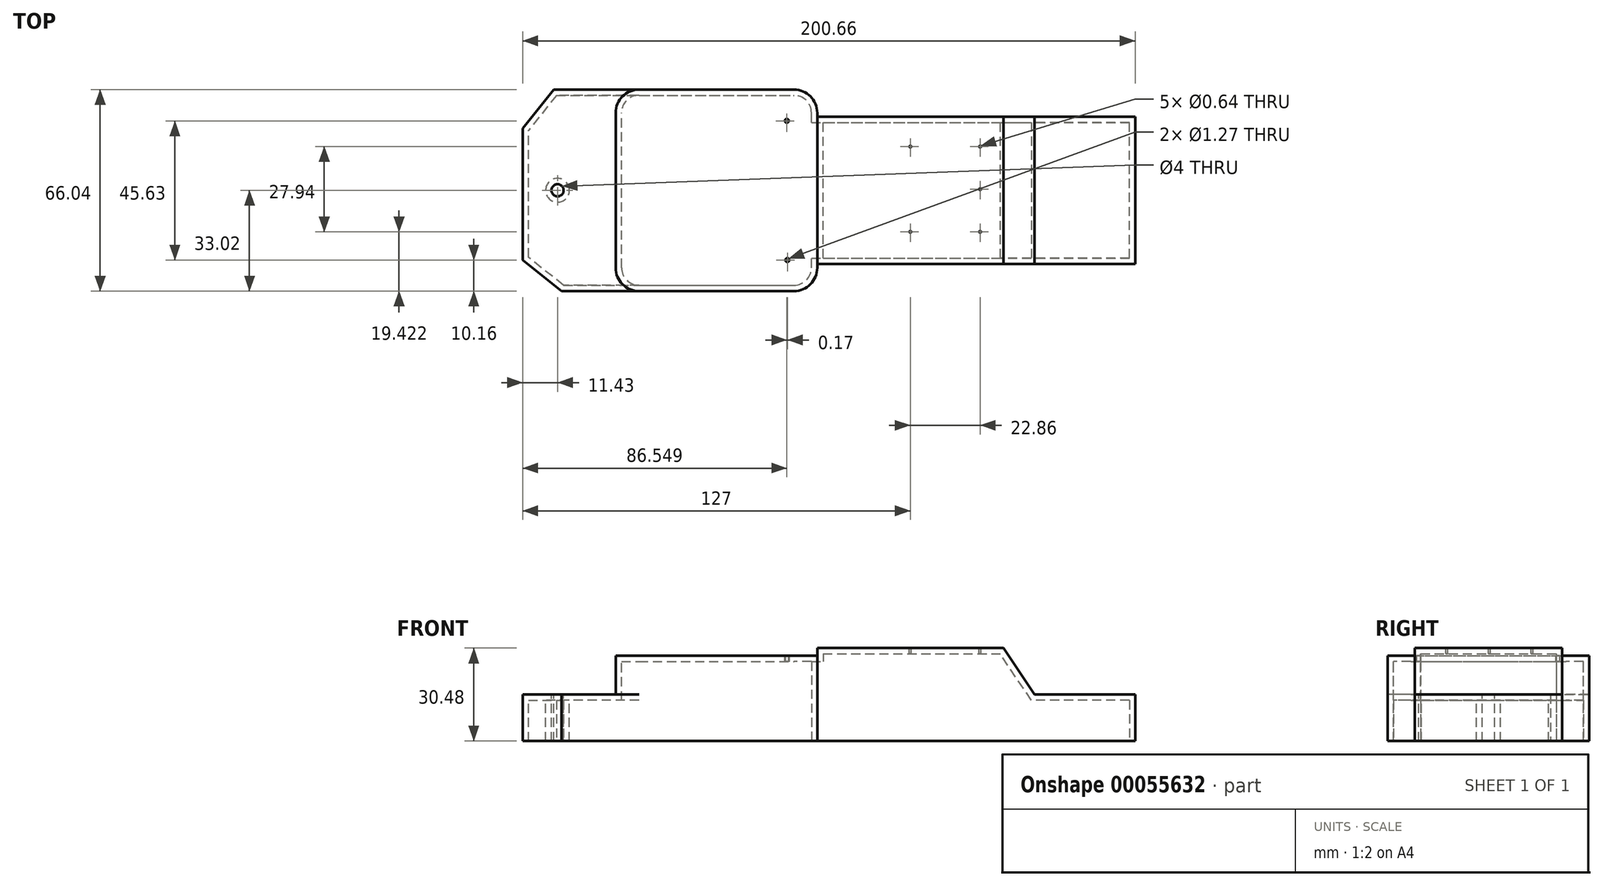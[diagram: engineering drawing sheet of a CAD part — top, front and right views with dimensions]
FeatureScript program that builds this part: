
annotation { "Feature Type Name" : "Feature", "Feature Type Description" : "" }
export const myFeature = defineFeature(function(context is Context, id is Id, definition is map)
    precondition{}
    {
        {
            var Q0;
            Q0=qCreatedBy(makeId("Top.planeOp"),FACE);
            var sketch = newSketch(context, id + "F0", { "sketchPlane" : qUnion([Q0])});
            skLineSegment(sketch, "E0.bottom", {"start": v(0, 0) * mm, "end": v(66.04, 0) * mm});
            skLineSegment(sketch, "E0.top", {"start": v(0, 66.04) * mm, "end": v(66.04, 66.04) * mm});
            skLineSegment(sketch, "E0.left", {"start": v(0, 0) * mm, "end": v(0, 66.04) * mm});
            skLineSegment(sketch, "E0.right", {"start": v(66.04, 0) * mm, "end": v(66.04, 66.04) * mm});
            skLineSegment(sketch, "E1.bottom", {"start": v(0, 0) * mm, "end": v(-30.48, 0) * mm});
            skLineSegment(sketch, "E1.top", {"start": v(0, 66.04) * mm, "end": v(-30.48, 66.04) * mm});
            skLineSegment(sketch, "E1.right", {"start": v(-30.48, 0) * mm, "end": v(-30.48, 66.04) * mm});
            skSolve(sketch);
        }
        {
            var Q0;
            Q0=makeQuery(id+"F0.imprint","IMPRINT",FACE,{"disambiguationData":[TD([[makeQuery(id+"F0.imprint","IMPRINT",EDGE,{"derivedFrom":sQuery(id+"F0.wireOp",EDGE,"E0.bottom")}),1.0]])]});
            extrude(context, id + "F1", {"entities" : qUnion([Q0]), "depth" : 27.94 * mm});
        }
        {
            var Q0;
            Q0=qCreatedBy(makeId("Top.planeOp"),FACE);
            var sketch = newSketch(context, id + "F2", { "sketchPlane" : qUnion([Q0])});
            skLineSegment(sketch, "E2.bottom", {"start": v(0, 0) * mm, "end": v(-30.48, 0) * mm});
            skLineSegment(sketch, "E2.top", {"start": v(0, 66.04) * mm, "end": v(-30.48, 66.04) * mm});
            skLineSegment(sketch, "E2.left", {"start": v(0, 0) * mm, "end": v(0, 66.04) * mm});
            skLineSegment(sketch, "E2.right", {"start": v(-30.48, 0) * mm, "end": v(-30.48, 66.04) * mm});
            skSolve(sketch);
        }
        {
            var Q0;
            Q0=makeQuery(id+"F2.imprint","IMPRINT",FACE,{"disambiguationData":[TD([[makeQuery(id+"F2.imprint","IMPRINT",EDGE,{"derivedFrom":sQuery(id+"F2.wireOp",EDGE,"E2.bottom")}),-1.0]])]});
            extrude(context, id + "F3", {"entities" : qUnion([Q0]), "operationType" : NewBodyOperationType.ADD, "depth" : 15.24 * mm});
        }
        {
            var Q0;
            Q0=qCreatedBy(makeId("Top.planeOp"),FACE);
            var sketch = newSketch(context, id + "F4", { "sketchPlane" : qUnion([Q0])});
            skLineSegment(sketch, "E3.bottom", {"start": v(66.04, 8.89) * mm, "end": v(137.16, 8.9) * mm});
            skLineSegment(sketch, "E3.top", {"start": v(66.04, 57.15) * mm, "end": v(137.16, 57.15) * mm});
            skLineSegment(sketch, "E3.left", {"start": v(66.04, 8.89) * mm, "end": v(66.04, 57.15) * mm});
            skLineSegment(sketch, "E3.right", {"start": v(137.16, 8.9) * mm, "end": v(137.16, 57.15) * mm});
            skSolve(sketch);
        }
        {
            var Q0;
            Q0 = qSketchRegion(id + "F4", true);
            var Q1;
            Q1=makeQuery(id+"F4.imprint","IMPRINT",FACE,{"disambiguationData":[TD([[makeQuery(id+"F4.imprint","IMPRINT",EDGE,{"derivedFrom":sQuery(id+"F4.wireOp",EDGE,"E3.bottom")}),1.0]])]});
            extrude(context, id + "F5", {"entities" : qUnion([Q0, Q1]), "operationType" : NewBodyOperationType.ADD, "depth" : 30.48 * mm});
        }
        {
            var Q0;
            Q0=makeQuery(id+"F3.opExtrude","SWEPT_EDGE",EDGE,{"disambiguationData":[OSD([sQuery(id+"F2.wireOp",EDGE,"E2.bottom"),sQuery(id+"F2.wireOp",EDGE,"E2.right")])]});
            chamfer(context, id + "F6", {"entities" : qUnion([Q0]), "chamferType" : ChamferType.TWO_OFFSETS, "width1" : 12.7 * mm, "oppositeDirection" : false, "width2" : 10.16 * mm, "tangentPropagation" : true});
        }
        {
            var Q0;
            Q0=makeQuery(id+"F3.opExtrude","SWEPT_EDGE",EDGE,{"disambiguationData":[OSD([sQuery(id+"F2.wireOp",EDGE,"E2.top"),sQuery(id+"F2.wireOp",EDGE,"E2.right")])]});
            chamfer(context, id + "F7", {"entities" : qUnion([Q0]), "chamferType" : ChamferType.TWO_OFFSETS, "width1" : 12.7 * mm, "oppositeDirection" : false, "width2" : 10.16 * mm, "tangentPropagation" : true});
        }
        {
            var Q0;
            Q0=makeQuery(id+"F1.opExtrude","SWEPT_EDGE",EDGE,{"disambiguationData":[OSD([sQuery(id+"F0.wireOp",EDGE,"E0.bottom"),sQuery(id+"F0.wireOp",EDGE,"E1.bottom"),sQuery(id+"F0.wireOp",EDGE,"E0.left")])]});
            var Q1;
            Q1=makeQuery(id+"F1.opExtrude","SWEPT_EDGE",EDGE,{"disambiguationData":[OSD([sQuery(id+"F0.wireOp",EDGE,"E0.top"),sQuery(id+"F0.wireOp",EDGE,"E1.top"),sQuery(id+"F0.wireOp",EDGE,"E0.left")])]});
            fillet(context, id + "F8", {"entities" : qUnion([Q0, Q1]), "radius" : 7.62 * mm, "tangentPropagation" : true, "allowEdgeOverflow" : false});
        }
        {
            var Q0;
            Q0=makeQuery(id+"F1.opExtrude","SWEPT_EDGE",EDGE,{"disambiguationData":[OSD([sQuery(id+"F0.wireOp",EDGE,"E0.top"),sQuery(id+"F0.wireOp",EDGE,"E0.right")])]});
            var Q1;
            Q1=makeQuery(id+"F1.opExtrude","SWEPT_EDGE",EDGE,{"disambiguationData":[OSD([sQuery(id+"F0.wireOp",EDGE,"E0.bottom"),sQuery(id+"F0.wireOp",EDGE,"E0.right")])]});
            fillet(context, id + "F9", {"entities" : qUnion([Q0, Q1]), "radius" : 7.62 * mm, "tangentPropagation" : true, "allowEdgeOverflow" : false});
        }
        {
            var Q0;
            Q0=makeQuery(id+"F5.opExtrude","CAP_EDGE",EDGE,{"disambiguationData":[OSD([sQuery(id+"F4.wireOp",EDGE,"E3.right")])],"isStart":false});
            chamfer(context, id + "F10", {"entities" : qUnion([Q0]), "chamferType" : ChamferType.TWO_OFFSETS, "width1" : 10.16 * mm, "oppositeDirection" : false, "width2" : 15.24 * mm, "tangentPropagation" : true});
        }
        {
            var Q0;
            Q0=makeQuery(id+"F5.opExtrude","SWEPT_FACE",FACE,{"disambiguationData":[OSD([sQuery(id+"F4.wireOp",EDGE,"E3.right")])]});
            extrude(context, id + "F11", {"entities" : qUnion([Q0]), "operationType" : NewBodyOperationType.ADD, "depth" : 33.02 * mm});
        }
        {
            var Q0;
            Q0=makeQuery(id+"F3.opExtrude","CAP_FACE",FACE,{"disambiguationData":[OSD([sQuery(id+"F2.wireOp",EDGE,"E2.bottom"),sQuery(id+"F2.wireOp",EDGE,"E2.top"),sQuery(id+"F2.wireOp",EDGE,"E2.left"),sQuery(id+"F2.wireOp",EDGE,"E2.right")])],"isStart":false});
            var sketch = newSketch(context, id + "F12", { "sketchPlane" : qUnion([Q0])});
            skCircle(sketch, "E4", {"center": v(-19.05, 33.02) * mm, "radius": 2.07 * mm});
            skSolve(sketch);
        }
        {
            var Q0;
            Q0=sQuery(id+"F12.wireOp",VERTEX,"E4.center");
            var Q1;
            Q1=makeQuery(id+"F1.opExtrude","SWEPT_BODY",BODY,{"disambiguationData":[OSD([sQuery(id+"F0.wireOp",EDGE,"E0.bottom"),sQuery(id+"F0.wireOp",EDGE,"E0.top"),sQuery(id+"F0.wireOp",EDGE,"E0.right"),sQuery(id+"F0.wireOp",EDGE,"E0.left")])]});
            hole(context, id + "F13", {"style" : HoleStyle.SIMPLE, "holeDiameter" : 4 * mm, "endStyle" : HoleEndStyle.THROUGH, "locations" : qUnion([Q0]), "scope" : qUnion([Q1])});
        }
        {
            var Q0;
            {var subQ0=sQuery(id+"F4.wireOp",EDGE,"E3.right");Q0=makeQuery(id+"F11.boolean.opBoolean","MERGE",FACE,{"derivedFrom":[makeQuery(id+"F5.boolean.opBoolean","MERGE",FACE,{"derivedFrom":[makeQuery(id+"F3.boolean.opBoolean","MERGE",FACE,{"derivedFrom":[makeQuery(id+"F1.opExtrude","CAP_FACE",FACE,{"disambiguationData":[OSD([sQuery(id+"F0.wireOp",EDGE,"E0.bottom"),sQuery(id+"F0.wireOp",EDGE,"E0.top"),sQuery(id+"F0.wireOp",EDGE,"E0.right"),sQuery(id+"F0.wireOp",EDGE,"E0.left")])],"isStart":true}),makeQuery(id+"F3.opExtrude","CAP_FACE",FACE,{"disambiguationData":[OSD([sQuery(id+"F2.wireOp",EDGE,"E2.bottom"),sQuery(id+"F2.wireOp",EDGE,"E2.top"),sQuery(id+"F2.wireOp",EDGE,"E2.left"),sQuery(id+"F2.wireOp",EDGE,"E2.right")])],"isStart":true})]}),makeQuery(id+"F5.opExtrude","CAP_FACE",FACE,{"disambiguationData":[OSD([sQuery(id+"F4.wireOp",EDGE,"E3.bottom"),sQuery(id+"F4.wireOp",EDGE,"E3.top"),sQuery(id+"F4.wireOp",EDGE,"E3.left"),subQ0])],"isStart":true})]}),makeQuery(id+"F11.opExtrude","SWEPT_FACE",FACE,{"disambiguationData":[OSD([subQ0]),TDD([makeQuery(id+"F5.opExtrude","CAP_EDGE",EDGE,{"disambiguationData":[OSD([subQ0])],"isStart":true})])]})]});}
            shell(context, id + "F14", {"entities" : qUnion([Q0]), "thickness" : 1.9 * mm});
        }
        {
            var Q0;
            Q0=makeQuery(id+"F1.opExtrude","CAP_FACE",FACE,{"disambiguationData":[OSD([sQuery(id+"F0.wireOp",EDGE,"E0.bottom"),sQuery(id+"F0.wireOp",EDGE,"E0.top"),sQuery(id+"F0.wireOp",EDGE,"E0.right"),sQuery(id+"F0.wireOp",EDGE,"E0.left")])],"isStart":false});
            var sketch = newSketch(context, id + "F15", { "sketchPlane" : qUnion([Q0])});
            skLineSegment(sketch, "E5.bottom", {"start": v(66.23, 65.95) * mm, "end": v(56.07, 65.95) * mm});
            skLineSegment(sketch, "E5.top", {"start": v(66.23, 55.8) * mm, "end": v(56.07, 55.8) * mm});
            skLineSegment(sketch, "E5.left", {"start": v(66.23, 65.95) * mm, "end": v(66.23, 55.8) * mm});
            skLineSegment(sketch, "E5.right", {"start": v(56.07, 65.95) * mm, "end": v(56.07, 55.8) * mm});
            skLineSegment(sketch, "E6.bottom", {"start": v(66.4, 0) * mm, "end": v(56.24, 0) * mm});
            skLineSegment(sketch, "E6.top", {"start": v(66.4, 10.16) * mm, "end": v(56.24, 10.16) * mm});
            skLineSegment(sketch, "E6.left", {"start": v(66.4, 0) * mm, "end": v(66.4, 10.16) * mm});
            skLineSegment(sketch, "E6.right", {"start": v(56.24, 0) * mm, "end": v(56.24, 10.16) * mm});
            skSolve(sketch);
        }
        {
            var Q0;
            Q0=sQuery(id+"F15.wireOp",VERTEX,"E6.top.end");
            var Q1;
            Q1=sQuery(id+"F15.wireOp",VERTEX,"E5.right.end");
            var Q2;
            Q2=makeQuery(id+"F1.opExtrude","SWEPT_BODY",BODY,{"disambiguationData":[OSD([sQuery(id+"F0.wireOp",EDGE,"E0.bottom"),sQuery(id+"F0.wireOp",EDGE,"E0.top"),sQuery(id+"F0.wireOp",EDGE,"E0.right"),sQuery(id+"F0.wireOp",EDGE,"E0.left")])]});
            hole(context, id + "F16", {"style" : HoleStyle.SIMPLE, "holeDiameter" : 1.27 * mm, "endStyle" : HoleEndStyle.THROUGH, "locations" : qUnion([Q0, Q1]), "scope" : qUnion([Q2])});
        }
        {
            var Q0;
            Q0=makeQuery(id+"F5.opExtrude","CAP_FACE",FACE,{"disambiguationData":[OSD([sQuery(id+"F4.wireOp",EDGE,"E3.bottom"),sQuery(id+"F4.wireOp",EDGE,"E3.top"),sQuery(id+"F4.wireOp",EDGE,"E3.left"),sQuery(id+"F4.wireOp",EDGE,"E3.right")])],"isStart":false});
            var sketch = newSketch(context, id + "F17", { "sketchPlane" : qUnion([Q0])});
            skLineSegment(sketch, "E7.bottom", {"start": v(96.52, 33.4) * mm, "end": v(119.38, 33.4) * mm});
            skLineSegment(sketch, "E7.top", {"start": v(96.52, 19.42) * mm, "end": v(119.38, 19.42) * mm});
            skLineSegment(sketch, "E7.left", {"start": v(96.52, 33.4) * mm, "end": v(96.52, 19.42) * mm});
            skLineSegment(sketch, "E7.right", {"start": v(119.38, 33.4) * mm, "end": v(119.38, 19.42) * mm});
            skLineSegment(sketch, "E8.MirrorCS", {"start": v(96.52, 33.4) * mm, "end": v(96.52, 47.36) * mm});
            skLineSegment(sketch, "E9.MirrorCS", {"start": v(119.38, 33.4) * mm, "end": v(119.38, 47.36) * mm});
            skLineSegment(sketch, "E10.MirrorCS", {"start": v(96.52, 47.36) * mm, "end": v(119.38, 47.36) * mm});
            skSolve(sketch);
        }
        {
            var Q0;
            Q0=sQuery(id+"F17.wireOp",VERTEX,"E10.MirrorCS.start");
            var Q1;
            Q1=sQuery(id+"F17.wireOp",VERTEX,"E9.MirrorCS.end");
            var Q2;
            Q2=sQuery(id+"F17.wireOp",VERTEX,"E7.right.start");
            var Q3;
            Q3=sQuery(id+"F17.wireOp",VERTEX,"E7.right.end");
            var Q4;
            Q4=sQuery(id+"F17.wireOp",VERTEX,"E7.left.end");
            var Q5;
            Q5=makeQuery(id+"F1.opExtrude","SWEPT_BODY",BODY,{"disambiguationData":[OSD([sQuery(id+"F0.wireOp",EDGE,"E0.bottom"),sQuery(id+"F0.wireOp",EDGE,"E0.top"),sQuery(id+"F0.wireOp",EDGE,"E0.right"),sQuery(id+"F0.wireOp",EDGE,"E0.left")])]});
            hole(context, id + "F18", {"style" : HoleStyle.SIMPLE, "holeDiameter" : 0.64 * mm, "endStyle" : HoleEndStyle.THROUGH, "locations" : qUnion([Q0, Q1, Q2, Q3, Q4]), "scope" : qUnion([Q5])});
        }
    });
